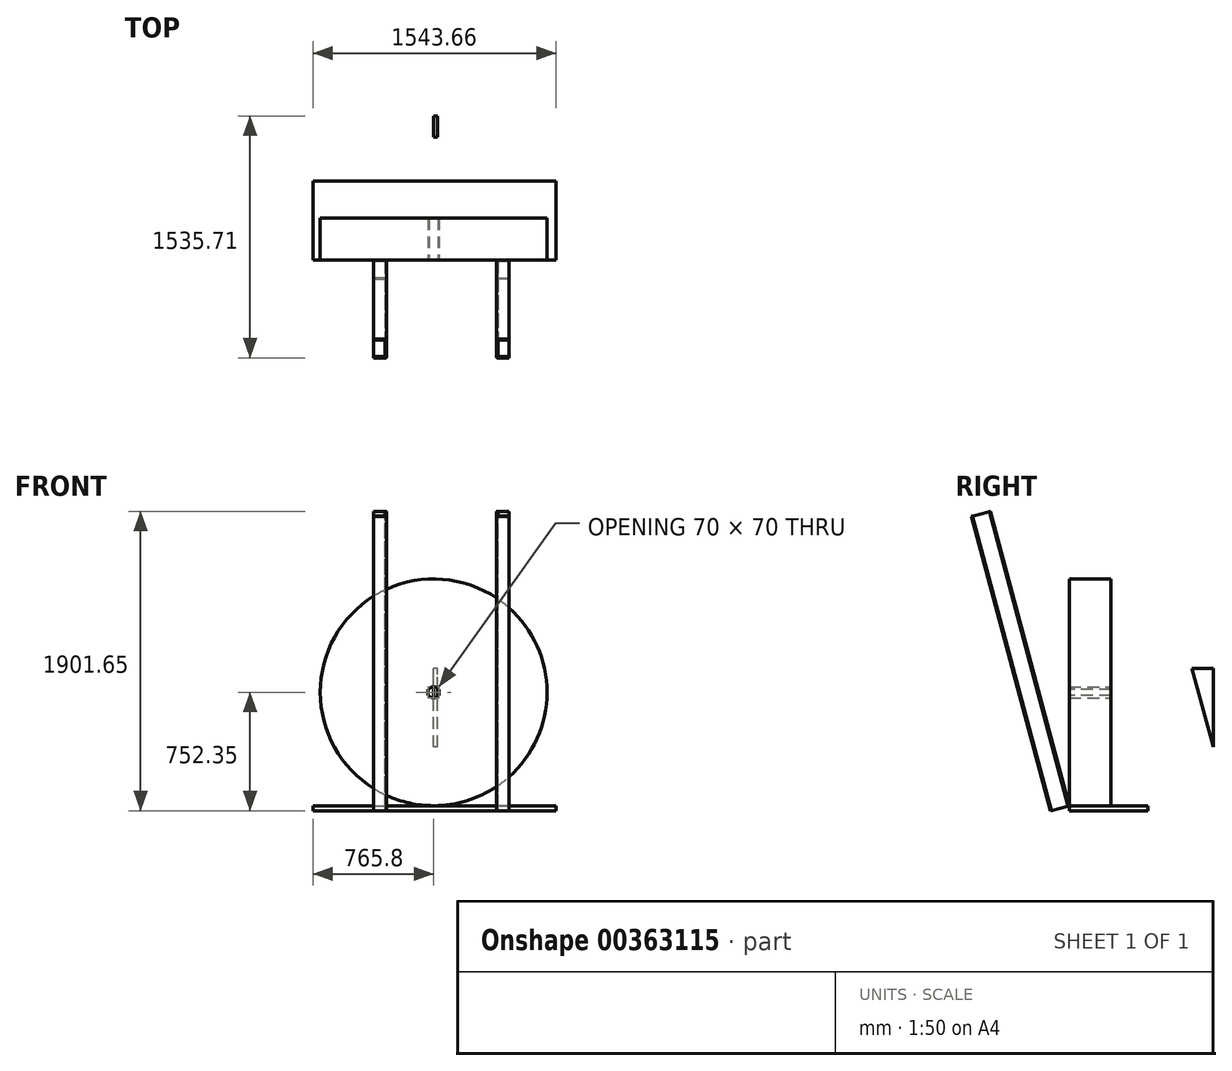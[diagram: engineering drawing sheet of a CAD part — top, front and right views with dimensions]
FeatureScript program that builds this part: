
annotation { "Feature Type Name" : "Feature", "Feature Type Description" : "" }
export const myFeature = defineFeature(function(context is Context, id is Id, definition is map)
    precondition{}
    {
        {
            var Q0;
            Q0=qCreatedBy(makeId("Front.planeOp"),FACE);
            var sketch = newSketch(context, id + "F0", { "sketchPlane" : qUnion([Q0])});
            skCircle(sketch, "E0", {"center": v(0, 0) * mm, "radius": 720 * mm});
            skLineSegment(sketch, "E1", {"start": v(-1092.76, 0) * mm, "end": v(1083.6, 0) * mm, "construction": true});
            skCircle(sketch, "E2", {"center": v(0, 0) * mm, "radius": 35 * mm});
            skSolve(sketch);
        }
        {
            var Q0;
            Q0=makeQuery(id+"F0.imprint","IMPRINT",FACE,{"disambiguationData":[TD([[makeQuery(id+"F0.imprint","IMPRINT",EDGE,{"derivedFrom":sQuery(id+"F0.wireOp",EDGE,"E0")}),1.0]])]});
            var Q1;
            Q1=sQuery(id+"F0.wireOp",EDGE,"E1");
            extrude(context, id + "F1", {"entities" : qUnion([Q0]), "surfaceEntities" : qUnion([Q1]), "depth" : 265 * mm});
        }
        {
            var Q0;
            Q0=makeQuery(id+"F1.opExtrude","CAP_FACE",FACE,{"disambiguationData":[OSD([sQuery(id+"F0.wireOp",EDGE,"E0"),sQuery(id+"F0.wireOp",EDGE,"E2")])],"isStart":false});
            var sketch = newSketch(context, id + "F2", { "sketchPlane" : qUnion([Q0])});
            skLineSegment(sketch, "E3", {"start": v(-900, 0) * mm, "end": v(900, 0) * mm, "construction": true});
            skLineSegment(sketch, "E4", {"start": v(0, 656.98) * mm, "end": v(0, -722.36) * mm, "construction": true});
            skLineSegment(sketch, "E5", {"start": v(-900, 20) * mm, "end": v(900, 20) * mm, "construction": true});
            skLineSegment(sketch, "E6", {"start": v(-903.02, -20) * mm, "end": v(1302.32, -20) * mm, "construction": true});
            skLineSegment(sketch, "E7", {"start": v(-720, -266.9) * mm, "end": v(-720, 307.42) * mm, "construction": true});
            skLineSegment(sketch, "E8", {"start": v(720, 321.7) * mm, "end": v(720, -335.48) * mm, "construction": true});
            skLineSegment(sketch, "E9", {"start": v(775, 316) * mm, "end": v(775, -329.77) * mm, "construction": true});
            skLineSegment(sketch, "E10.bottom", {"start": v(-720, 0) * mm, "end": v(775, 0) * mm});
            skLineSegment(sketch, "E10.top", {"start": v(-720, 20) * mm, "end": v(775, 20) * mm});
            skLineSegment(sketch, "E10.left", {"start": v(-720, 0) * mm, "end": v(-720, 20) * mm});
            skLineSegment(sketch, "E10.right", {"start": v(775, 0) * mm, "end": v(775, 20) * mm});
            skLineSegment(sketch, "E11.bottom", {"start": v(-720, -20) * mm, "end": v(775, -20) * mm});
            skLineSegment(sketch, "E11.left", {"start": v(-720, -20) * mm, "end": v(-720, 0) * mm});
            skLineSegment(sketch, "E11.right", {"start": v(775, -20) * mm, "end": v(775, 0) * mm});
            skLineSegment(sketch, "E12", {"start": v(-35, 20) * mm, "end": v(-35, -20) * mm});
            skLineSegment(sketch, "E13", {"start": v(35, 20) * mm, "end": v(35, -20) * mm});
            skSolve(sketch);
        }
        {
            var Q0;
            Q0=makeQuery(id+"FSUQJoN1h2uHWWV_1.opExtrude","CAP_FACE",FACE,{"disambiguationData":[OSD([sQuery(id+"F0.wireOp",EDGE,"E2"),sQuery(id+"F2.wireOp",EDGE,"E10.top"),sQuery(id+"F2.wireOp",EDGE,"E10.bottom")])],"isStart":false});
            var Q1;
            {var subQ0=sQuery(id+"F2.wireOp",EDGE,"E13");var subQ1=sQuery(id+"F2.wireOp",EDGE,"E10.top");var subQ2=makeQuery(id+"F2.imprint","INTERSECT",VERTEX,{"derivedFrom":[subQ1,subQ0]});Q1=makeQuery(id+"F2.imprint","IMPRINT",FACE,{"disambiguationData":[TD([[makeQuery(id+"F2.imprint","IMPRINT",EDGE,{"disambiguationData":[TD([[subQ2,1.0]])],"derivedFrom":subQ1}),-1.0]])]});}
            var Q2;
            {var subQ0=sQuery(id+"F2.wireOp",EDGE,"E13");var subQ1=sQuery(id+"F2.wireOp",EDGE,"E11.bottom");var subQ2=makeQuery(id+"F2.imprint","INTERSECT",VERTEX,{"derivedFrom":[subQ1,subQ0]});Q2=makeQuery(id+"F2.imprint","IMPRINT",FACE,{"disambiguationData":[TD([[makeQuery(id+"F2.imprint","IMPRINT",EDGE,{"disambiguationData":[TD([[subQ2,1.0]])],"derivedFrom":subQ1}),1.0]])]});}
            var Q3;
            {var subQ0=sQuery(id+"F2.wireOp",EDGE,"E12");var subQ1=sQuery(id+"F2.wireOp",EDGE,"E11.bottom");var subQ2=makeQuery(id+"F2.imprint","INTERSECT",VERTEX,{"derivedFrom":[subQ1,subQ0]});Q3=makeQuery(id+"F2.imprint","IMPRINT",FACE,{"disambiguationData":[TD([[makeQuery(id+"F2.imprint","IMPRINT",EDGE,{"disambiguationData":[TD([[subQ2,-1.0]])],"derivedFrom":subQ1}),1.0]])]});}
            var Q4;
            {var subQ0=sQuery(id+"F2.wireOp",EDGE,"E12");var subQ1=sQuery(id+"F2.wireOp",EDGE,"E10.top");var subQ2=makeQuery(id+"F2.imprint","INTERSECT",VERTEX,{"derivedFrom":[subQ1,subQ0]});Q4=makeQuery(id+"F2.imprint","IMPRINT",FACE,{"disambiguationData":[TD([[makeQuery(id+"F2.imprint","IMPRINT",EDGE,{"disambiguationData":[TD([[subQ2,-1.0]])],"derivedFrom":subQ1}),-1.0]])]});}
            var Q5;
            Q5=makeQuery(id+"FGY7fiWuK6QfrZZ_1.opExtrude","CAP_FACE",FACE,{"disambiguationData":[OSD([sQuery(id+"F0.wireOp",EDGE,"E2"),sQuery(id+"F2.wireOp",EDGE,"E11.bottom"),sQuery(id+"F2.wireOp",EDGE,"E10.bottom")])],"isStart":false});
            extrude(context, id + "F3", {"entities" : qUnion([Q0, Q1, Q2, Q3, Q4, Q5]), "operationType" : NewBodyOperationType.REMOVE, "endBound" : BoundingType.THROUGH_ALL, "oppositeDirection" : true, "depth" : 25 * mm});
        }
        {
            var Q0;
            {var subQ0=sQuery(id+"F2.wireOp",EDGE,"E11.bottom");var subQ7=makeQuery(id+"F2.imprint","INTERSECT",VERTEX,{"derivedFrom":[subQ0,sQuery(id+"F2.wireOp",EDGE,"E12")]});Q0=makeQuery(id+"F2.imprint","IMPRINT",FACE,{"disambiguationData":[TD([[makeQuery(id+"F2.imprint","IMPRINT",EDGE,{"disambiguationData":[TD([[subQ7,1.0]])],"derivedFrom":subQ0}),-1.0]])]});}
            var sketch = newSketch(context, id + "F4", { "sketchPlane" : qUnion([Q0])});
            skLineSegment(sketch, "E14", {"start": v(-831.4, -720) * mm, "end": v(820.31, -720) * mm, "construction": true});
            skLineSegment(sketch, "E15.bottom", {"start": v(-765.8, -720) * mm, "end": v(777.86, -720) * mm});
            skLineSegment(sketch, "E15.top", {"start": v(-765.8, -752.3) * mm, "end": v(777.86, -752.3) * mm});
            skLineSegment(sketch, "E15.left", {"start": v(-765.8, -720) * mm, "end": v(-765.8, -752.3) * mm});
            skLineSegment(sketch, "E15.right", {"start": v(777.86, -720) * mm, "end": v(777.86, -752.3) * mm});
            skSolve(sketch);
        }
        {
            var Q0;
            Q0 = qSketchRegion(id + "F4", true);
            extrude(context, id + "F5", {"entities" : qUnion([Q0]), "operationType" : NewBodyOperationType.ADD, "depth" : -500 * mm});
        }
        {
            var Q0;
            Q0=qCreatedBy(makeId("Right.planeOp"),FACE);
            var sketch = newSketch(context, id + "F6", { "sketchPlane" : qUnion([Q0])});
            skLineSegment(sketch, "E16.0", {"start": v(-265, -720) * mm, "end": v(-265, -752.3) * mm});
            skLineSegment(sketch, "E17.0", {"start": v(235, -720) * mm, "end": v(-265, -720) * mm});
            skLineSegment(sketch, "E18", {"start": v(-265, -720) * mm, "end": v(-900.32, 1651.04) * mm, "construction": true});
            skArc(sketch, "E19", {"start": v(-900.32, 1651.04) * mm, "mid": v(-585.4, 1713.68) * mm, "end": v(-265, 1734.68) * mm, "construction": true});
            skLineSegment(sketch, "E20", {"start": v(-265, -720) * mm, "end": v(-265, 1734.68) * mm, "construction": true});
            skLineSegment(sketch, "E21", {"start": v(-265, -752.3) * mm, "end": v(-256.34, -752.3) * mm});
            skLineSegment(sketch, "E22", {"start": v(-265, -720) * mm, "end": v(-385.74, -752.35) * mm});
            skLineSegment(sketch, "E23", {"start": v(-385.74, -752.35) * mm, "end": v(-886.62, 1116.95) * mm});
            skLineSegment(sketch, "E24", {"start": v(-886.62, 1116.95) * mm, "end": v(-765.88, 1149.3) * mm});
            skLineSegment(sketch, "E25", {"start": v(-765.88, 1149.3) * mm, "end": v(-265, -720) * mm});
            skSolve(sketch);
        }
        {
            var Q0;
            Q0=makeQuery(id+"F6.imprint","IMPRINT",FACE,{"disambiguationData":[TD([[makeQuery(id+"F6.imprint","IMPRINT",EDGE,{"derivedFrom":sQuery(id+"F6.wireOp",EDGE,"E22")}),-1.0]])]});
            extrude(context, id + "F7", {"entities" : qUnion([Q0]), "depth" : -380 * mm, "hasSecondDirection" : true, "secondDirectionOppositeDirection" : true, "secondDirectionDepth" : 300 * mm});
        }
        {
            var Q0;
            Q0 = qSketchRegion(id + "F6", true);
            extrude(context, id + "F8", {"entities" : qUnion([Q0]), "depth" : 480 * mm, "hasSecondDirection" : true, "secondDirectionOppositeDirection" : true, "secondDirectionDepth" : -400 * mm});
        }
        {
            var Q0;
            Q0=makeQuery(id+"F7.opExtrude","SWEPT_FACE",FACE,{"disambiguationData":[OSD([sQuery(id+"F6.wireOp",EDGE,"E24")])]});
            var sketch = newSketch(context, id + "F9", { "sketchPlane" : qUnion([Q0])});
            skLineSegment(sketch, "E26.bottom", {"start": v(-380, -442.32) * mm, "end": v(-300, -442.32) * mm, "construction": true});
            skLineSegment(sketch, "E26.top", {"start": v(-375, -567.32) * mm, "end": v(-300, -567.32) * mm, "construction": true});
            skLineSegment(sketch, "E26.left", {"start": v(-380, -442.32) * mm, "end": v(-380, -562.32) * mm});
            skLineSegment(sketch, "E26.right", {"start": v(-300, -442.32) * mm, "end": v(-300, -567.32) * mm, "construction": true});
            skPoint(sketch, "E27.visualSharp", {"position": v(-380, -567.32) * mm});
            skLineSegment(sketch, "E28", {"start": v(-380, -450.32) * mm, "end": v(-308, -450.32) * mm});
            skLineSegment(sketch, "E29", {"start": v(-308, -450.32) * mm, "end": v(-308, -559.32) * mm});
            skLineSegment(sketch, "E30", {"start": v(-308, -559.32) * mm, "end": v(-380, -559.32) * mm});
            skLineSegment(sketch, "E31.0", {"start": v(480, -567.32) * mm, "end": v(480, -442.32) * mm});
            skLineSegment(sketch, "E32.0", {"start": v(480, -442.32) * mm, "end": v(400, -442.32) * mm, "construction": true});
            skLineSegment(sketch, "E33.0", {"start": v(400, -567.32) * mm, "end": v(400, -442.32) * mm, "construction": true});
            skLineSegment(sketch, "E34.0", {"start": v(480, -567.32) * mm, "end": v(400, -567.32) * mm, "construction": true});
            skLineSegment(sketch, "E35.bottom", {"start": v(480, -450.32) * mm, "end": v(408, -450.32) * mm});
            skLineSegment(sketch, "E35.top", {"start": v(480, -559.32) * mm, "end": v(408, -559.32) * mm});
            skLineSegment(sketch, "E35.left", {"start": v(480, -450.32) * mm, "end": v(480, -559.32) * mm});
            skLineSegment(sketch, "E35.right", {"start": v(408, -450.32) * mm, "end": v(408, -559.32) * mm});
            skSolve(sketch);
        }
        {
            var Q0;
            Q0=makeQuery(id+"F9.imprint","IMPRINT",FACE,{"disambiguationData":[TD([[makeQuery(id+"F9.imprint","IMPRINT",EDGE,{"derivedFrom":sQuery(id+"F9.wireOp",EDGE,"E35.bottom")}),1.0]])]});
            var Q1;
            {var subQ0=sQuery(id+"F9.wireOp",EDGE,"E28");Q1=makeQuery(id+"F9.imprint","IMPRINT",FACE,{"disambiguationData":[TD([[makeQuery(id+"F9.imprint","IMPRINT",EDGE,{"derivedFrom":subQ0}),-1.0]])]});}
            var Q2;
            Q2=sQuery(id+"F9.wireOp",EDGE,"E26.bottom");
            var Q3;
            Q3=sQuery(id+"F9.wireOp",EDGE,"E26.right");
            var Q4;
            Q4=sQuery(id+"F9.wireOp",EDGE,"E26.top");
            var Q5;
            Q5=sQuery(id+"F9.wireOp",EDGE,"E32.0");
            var Q6;
            Q6=sQuery(id+"F9.wireOp",EDGE,"E33.0");
            var Q7;
            Q7=sQuery(id+"F9.wireOp",EDGE,"E34.0");
            extrude(context, id + "F10", {"entities" : qUnion([Q0, Q1]), "operationType" : NewBodyOperationType.REMOVE, "surfaceEntities" : qUnion([Q2, Q3, Q4, Q5, Q6, Q7]), "endBound" : BoundingType.THROUGH_ALL, "oppositeDirection" : true, "depth" : 25 * mm});
        }
        {
            var Q0;
            {var subQ0=sQuery(id+"F9.wireOp",EDGE,"E28");var subQ1=sQuery(id+"F9.wireOp",EDGE,"E29");Q0=makeQuery(id+"F10.boolean.opBoolean","COPY",EDGE,{"disambiguationData":[TD([makeQuery(id+"F7.opExtrude","SWEPT_FACE",FACE,{"disambiguationData":[OSD([sQuery(id+"F6.wireOp",EDGE,"E22")])]})])],"derivedFrom":makeQuery(id+"F10.opExtrude","SWEPT_EDGE",EDGE,{"disambiguationData":[OSD([subQ0,subQ1])]})});}
            var Q1;
            Q1=makeQuery(id+"F8.opExtrude","CAP_EDGE",EDGE,{"disambiguationData":[OSD([sQuery(id+"F6.wireOp",EDGE,"E25")])],"isStart":true});
            var Q2;
            Q2=makeQuery(id+"F8.opExtrude","CAP_EDGE",EDGE,{"disambiguationData":[OSD([sQuery(id+"F6.wireOp",EDGE,"E23")])],"isStart":true});
            fillet(context, id + "F11", {"entities" : qUnion([Q0, Q1, Q2]), "radius" : 5 * mm, "tangentPropagation" : true, "allowEdgeOverflow" : false});
        }
        {
            var Q0;
            Q0=makeQuery(id+"F7.opExtrude","CAP_EDGE",EDGE,{"disambiguationData":[OSD([sQuery(id+"F6.wireOp",EDGE,"E23")])],"isStart":true});
            var Q1;
            Q1=makeQuery(id+"F7.opExtrude","CAP_EDGE",EDGE,{"disambiguationData":[OSD([sQuery(id+"F6.wireOp",EDGE,"E25")])],"isStart":true});
            fillet(context, id + "F12", {"entities" : qUnion([Q0, Q1]), "radius" : 5 * mm, "tangentPropagation" : true, "allowEdgeOverflow" : false});
        }
        {
            var Q0;
            Q0=makeQuery(id+"F10.boolean.opBoolean","COPY",EDGE,{"derivedFrom":makeQuery(id+"F10.opExtrude","SWEPT_EDGE",EDGE,{"disambiguationData":[OSD([sQuery(id+"F9.wireOp",EDGE,"E29"),sQuery(id+"F9.wireOp",EDGE,"E30")])]})});
            fillet(context, id + "F13", {"entities" : qUnion([Q0]), "radius" : 5 * mm, "tangentPropagation" : true, "allowEdgeOverflow" : false});
        }
        {
            var Q0;
            {var subQ0=sQuery(id+"F9.wireOp",EDGE,"E35.bottom");var subQ1=sQuery(id+"F9.wireOp",EDGE,"E35.right");Q0=makeQuery(id+"F10.boolean.opBoolean","COPY",EDGE,{"disambiguationData":[TD([makeQuery(id+"F8.opExtrude","SWEPT_FACE",FACE,{"disambiguationData":[OSD([sQuery(id+"F6.wireOp",EDGE,"E22")])]})])],"derivedFrom":makeQuery(id+"F10.opExtrude","SWEPT_EDGE",EDGE,{"disambiguationData":[OSD([subQ0,subQ1])]})});}
            fillet(context, id + "F14", {"entities" : qUnion([Q0]), "radius" : 5 * mm, "tangentPropagation" : true, "allowEdgeOverflow" : false});
        }
        {
            var Q0;
            Q0=makeQuery(id+"F10.boolean.opBoolean","COPY",EDGE,{"derivedFrom":makeQuery(id+"F10.opExtrude","SWEPT_EDGE",EDGE,{"disambiguationData":[OSD([sQuery(id+"F9.wireOp",EDGE,"E35.top"),sQuery(id+"F9.wireOp",EDGE,"E35.right")])]})});
            fillet(context, id + "F15", {"entities" : qUnion([Q0]), "radius" : 5 * mm, "tangentPropagation" : true, "allowEdgeOverflow" : false});
        }
        {
            var Q0;
            Q0=qCreatedBy(makeId("Right.planeOp"),FACE);
            var sketch = newSketch(context, id + "F16", { "sketchPlane" : qUnion([Q0])});
            skLineSegment(sketch, "E36", {"start": v(649.09, -378.58) * mm, "end": v(649.09, 500.54) * mm});
            skLineSegment(sketch, "E37", {"start": v(649.09, -347) * mm, "end": v(515.12, 153) * mm});
            skLineSegment(sketch, "E38", {"start": v(515.12, 153) * mm, "end": v(649.09, 153) * mm});
            skSolve(sketch);
        }
        {
            var Q0;
            Q0 = qSketchRegion(id + "F16", true);
            extrude(context, id + "F17", {"entities" : qUnion([Q0]), "depth" : 25 * mm});
        }
    });
